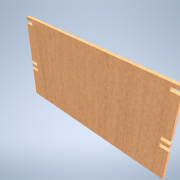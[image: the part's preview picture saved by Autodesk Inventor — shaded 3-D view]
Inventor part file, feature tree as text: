
AUTODESK INVENTOR PART (.ipt)
format: ipt  version: 2021 (Build 250183000, 183)  size: 167,936 bytes
history: native  units: mm
features: sketch x3, extrude x2
ambient origin geometry x8: Origin, YZ Plane, XZ Plane, XY Plane, X Axis, Y Axis, Z Axis, Center Point
bodies: Solid1 (feature_tree)
feature tree (5):
  extrude  "Extrusion1"  Depth=77.0mm
  extrude  "Extrusion4"  Depth=7.0mm
  sketch  "Sketch1"  dims[d0=144.0mm d1=77.0mm]
  sketch  "Sketch3"  dims[d2=3.0mm d3=0.0mm d27=7.0mm]
  sketch  "Sketch4"  dims[d28=3.0mm d29=20.0mm d31=137.0mm d32=20.0mm d34=38.0mm d37=0.0mm d38=0.0mm d39=20.0mm d41=6.0mm d42=20.0mm d44=137.0mm d47=50.0mm d48=10.0mm d49=1.5mm d50=0.0mm]
